# Revit family: Cabinet Linkeo DC width 800
name_source: partatom
category: Equipement spécialisé
units: mm (PartAtom-declared; Revit-internal decimal feet)

## family parameters
Basée sur le plan de construction = Non
Cote de connecteur circulaire = Utiliser le diamètre
Couper avec des vides une fois chargée = Non
Partagée = Oui
Point de calcul de pièce = Non
Toujours verticalement = Oui
Type d'élément = Normal

## types (4) — shared parameters
Application class = EC002499
Avec porte frontale = Oui
Color = IDS_NOIR
Degree of protection IK = IK02
Degree of protection IP = IP20
Distance of the aperture 1 = 275 mm
E-catalogue link = https://www.legrand.fr
Front door material = IDS_ACIER
Function = Server cabinets Linkeo DC
Locking of the front door = Three points
Material = Steel
Max load capacity = 1500
Model = With permanent frame
Model width = 800 mm  [stored 2.62467 ft]
Modular spacing = 19 inches
Mounting level = Front and rear
Number of doors = 1
Operating temperature = -25°C à 70°C
RAL Number = 9005
Rack location = 93 mm  [stored 0.305118 ft]
Storage temperature = -25°C à 70°C
Type of surface = Powder coating
Type of ventilation = Passive
Usable height (mm) = 1881 mm  [stored 6.17126 ft]
Width (mm) = 800 mm  [stored 2.62467 ft]
With earthing = Oui
With roof plate = Oui
zero-valued in all types: Elévation par défaut

## per-type parameters (varying)
| type | BIM wording | Depth | Depth of the model (mm) | Height | Legrand part number | Model height | Number of height units | Usable width (mm) |
| Cabinet Linkeo2 42U 800x1000 | Cabinet Linkeo2 42U 800x1000 equipped | 1000 mm  [stored 3.28084 ft] | 1000 mm  [stored 3.28084 ft] | 2047 mm  [stored 6.71588 ft] | 446802 | 1965 mm  [stored 6.44685 ft] | 42 | 890 mm  [stored 2.91995 ft] |
| Cabinet Linkeo2 42U 800x1200 | Cabinet Linkeo2 42U 800x1200 equipped | 1200 mm | 1200 mm | 2047 mm  [stored 6.71588 ft] | 446803 | 1965 mm  [stored 6.44685 ft] | 42 | 1090 mm  [stored 3.57612 ft] |
| Cabinet Linkeo2 47U 800x1000 | Cabinet Linkeo2 47U 800x1000 equipped | 1000 mm  [stored 3.28084 ft] | 1000 mm  [stored 3.28084 ft] | 2269 mm | 446806 | 2190 mm  [stored 7.18504 ft] | 47 | 890 mm  [stored 2.91995 ft] |
| Cabinet Linkeo2 47U 800x1200 | Cabinet Linkeo2 47U 800x1200 equipped | 1200 mm | 1200 mm | 2269 mm | 446807 | 2190 mm  [stored 7.18504 ft] | 47 | 1090 mm  [stored 3.57612 ft] |

note: [stored X ft] marks values corroborated as IEEE doubles in the binary element streams (Revit-internal decimal feet)
